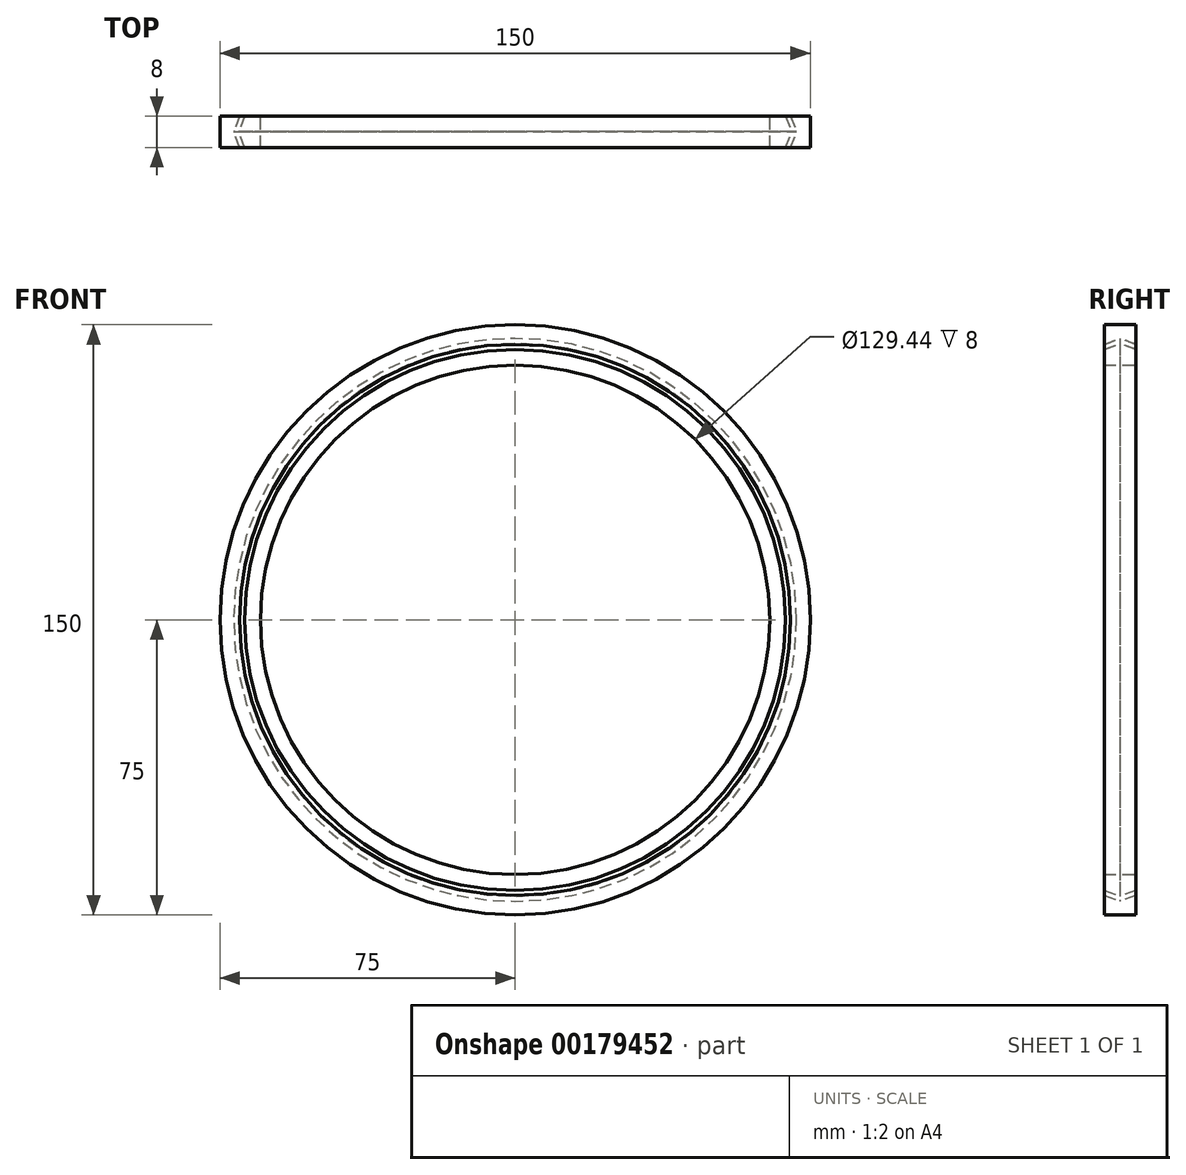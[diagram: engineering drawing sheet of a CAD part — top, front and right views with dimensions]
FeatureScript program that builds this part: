
annotation { "Feature Type Name" : "Feature", "Feature Type Description" : "" }
export const myFeature = defineFeature(function(context is Context, id is Id, definition is map)
    precondition{}
    {
        {
            var Q0;
            Q0=qCreatedBy(makeId("Front.planeOp"),FACE);
            var sketch = newSketch(context, id + "F0", { "sketchPlane" : qUnion([Q0])});
            skCircle(sketch, "E0", {"center": v(0, 0) * mm, "radius": 75 * mm});
            skCircle(sketch, "E1", {"center": v(0, 0) * mm, "radius": 70 * mm});
            skSolve(sketch);
        }
        {
            var Q0;
            Q0=qCreatedBy(makeId("Top.planeOp"),FACE);
            var sketch = newSketch(context, id + "F1", { "sketchPlane" : qUnion([Q0])});
            skLineSegment(sketch, "E2", {"start": v(-70, 0) * mm, "end": v(-71.5, -4) * mm});
            skLineSegment(sketch, "E3", {"start": v(-71.5, -4) * mm, "end": v(-70, -8) * mm});
            skLineSegment(sketch, "E4", {"start": v(-70, -8) * mm, "end": v(-75, -8) * mm});
            skLineSegment(sketch, "E5", {"start": v(-75, -8) * mm, "end": v(-75, 0) * mm});
            skLineSegment(sketch, "E6", {"start": v(-75, 0) * mm, "end": v(-70, 0) * mm});
            skLineSegment(sketch, "E7.0", {"start": v(-70.22, -4) * mm, "end": v(-68.72, -8) * mm});
            skLineSegment(sketch, "E7.1", {"start": v(-68.72, 0) * mm, "end": v(-70.22, -4) * mm});
            skLineSegment(sketch, "E8", {"start": v(-68.72, -8) * mm, "end": v(-64.72, -8) * mm});
            skLineSegment(sketch, "E9", {"start": v(-68.72, 0) * mm, "end": v(-64.72, 0) * mm});
            skLineSegment(sketch, "E10", {"start": v(-64.72, 0) * mm, "end": v(-64.72, -8) * mm});
            skSolve(sketch);
        }
        {
            var Q0;
            Q0=qCreatedBy(makeId("Top.planeOp"),FACE);
            var sketch = newSketch(context, id + "F2", { "sketchPlane" : qUnion([Q0])});
            skLineSegment(sketch, "E11", {"start": v(0, 0) * mm, "end": v(0, -31) * mm, "construction": true});
            skSolve(sketch);
        }
        {
            var Q0;
            Q0 = qSketchRegion(id + "F1", true);
            var Q1;
            Q1=sQuery(id+"F2.wireOp",EDGE,"E11");
            revolve(context, id + "F3", {"entities" : qUnion([Q0]), "axis" : qUnion([Q1]), "revolveType" : RevolveType.FULL});
        }
    });
